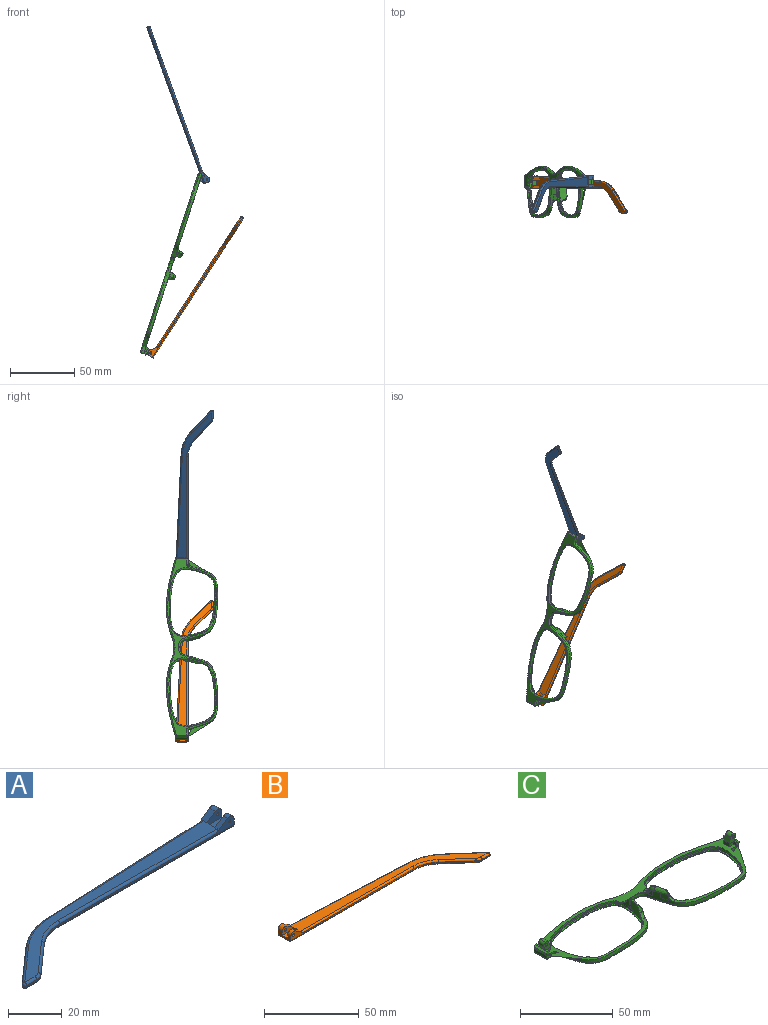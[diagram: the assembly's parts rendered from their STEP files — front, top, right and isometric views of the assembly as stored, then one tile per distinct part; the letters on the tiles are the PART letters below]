
ASSEMBLY  parts=3 mates=2
PART A: 43 faces, bbox 130.2x29.5x5.9 mm
  f0: plane 9.62x3.72mm, normal (1,0,0), area 24.7mm2, adj f1,f3,f4,f5,f10,f16,f18,f28
  f1: cylinder r=2.2mm len=3.45mm, axis (0,-1,0), area 11mm2, adj f0,f2,f4,f37
  f2: plane 6.01x3.91mm, normal (-0.55,0,0.84), area 12.7mm2, adj f1,f4,f9,f19,f37
  f3: plane 2.26x0.1mm, normal (0,0,1), area 0.1mm2, adj f0,f5,f18
  f4: plane 92.1x4.9mm, normal (0,-1,0), area 79.9mm2, adj f0,f1,f2,f14,f19,f36,f42
  f5: plane 93.42x4.13mm, normal (-0.04,1,0), area 64.8mm2, adj f0,f3,f11,f15,f17,f27,f28
  f6: plane 17.82x15.72mm, normal (-0.66,0.75,0), area 14.3mm2, adj f11,f12,f25,f30
  f7: plane 5.46x0.6mm, normal (0,-1,0), area 3.3mm2, adj f12,f13,f23,f32
  f8: plane 14.99x13.23mm, normal (0.66,-0.75,0), area 12mm2, adj f13,f14,f21,f34
  f9: plane 121.18x26.73mm, normal (0,0,1), area 627.7mm2, adj f2,f17,f19,f20,f21,f22,f23,f25
  f10: plane 129.1x27.08mm, normal (0,0,-1), area 686.5mm2, adj f0,f28,f29,f30,f32,f33,f34,f35
  f11: cylinder r=30mm len=18.52mm, axis (0,0,-1), area 12.2mm2, adj f5,f6,f26,f29
  f12: cylinder r=1mm len=1.75mm, axis (0,0,-1), area 1.5mm2, adj f6,f7,f24,f31
  f13: cylinder r=5mm len=3.31mm, axis (0,0,-1), area 2.2mm2, adj f7,f8,f22,f33
  f14: cylinder r=20mm len=13.23mm, axis (0,0,1), area 8.7mm2, adj f4,f8,f20,f35
  f15: plane 5.66x0.25mm, normal (0,0,-1), area 0.7mm2, adj f5,f17,f18
  f16: cylinder r=2.2mm len=3.45mm, axis (0,-1,0), area 14.8mm2, adj f0,f17,f18,f38
  f17: plane 6.01x3.91mm, normal (-0.55,0,0.84), area 16.9mm2, adj f5,f9,f15,f16,f18,f27,f38
  f18: plane 7.92x3.3mm, normal (0,1,0), area 15.9mm2, adj f0,f3,f15,f16,f17,f41
  f19: cylinder r=1mm len=84.18mm, axis (-1,0,0), area 131.4mm2, adj f2,f4,f9,f20
  f20: torus R=21mm, axis (0,0,1), area 23.1mm2, adj f9,f14,f19,f21
  f21: cylinder r=1mm len=15.65mm, axis (-0.75,-0.66,0), area 31.4mm2, adj f8,f9,f20,f22
  f22: torus R=4mm, axis (0,0,1), area 5.3mm2, adj f9,f13,f21,f23
  f23: cylinder r=1mm len=5.46mm, axis (-1,0,0), area 8.6mm2, adj f7,f9,f22,f24
  f24: sphere r=1mm, area 2.4mm2, adj f12,f23,f25
  f25: cylinder r=1mm len=18.48mm, axis (0.75,0.66,0), area 37.3mm2, adj f6,f9,f24,f26
  f26: torus R=29mm, axis (0,0,1), area 31.6mm2, adj f9,f11,f25,f27
  f27: cylinder r=1mm len=85.5mm, axis (1,0.04,0), area 133.5mm2, adj f5,f9,f17,f26
  f28: cylinder r=1mm len=93.46mm, axis (-1,-0.04,0), area 146.9mm2, adj f0,f5,f10,f29
  f29: torus R=29mm, axis (0,0,1), area 31.6mm2, adj f10,f11,f28,f30
  f30: cylinder r=1mm len=18.48mm, axis (-0.75,-0.66,0), area 37.3mm2, adj f6,f10,f29,f31
  f31: sphere r=1mm, area 2.4mm2, adj f12,f30,f32
  f32: cylinder r=1mm len=5.46mm, axis (1,0,0), area 8.6mm2, adj f7,f10,f31,f33
  f33: torus R=4mm, axis (0,0,1), area 5.3mm2, adj f10,f13,f32,f34
  f34: cylinder r=1mm len=15.65mm, axis (0.75,0.66,0), area 31.4mm2, adj f8,f10,f33,f35
  f35: torus R=21mm, axis (0,0,1), area 23.1mm2, adj f10,f14,f34,f36
  f36: cylinder r=1mm len=92.1mm, axis (1,0,0), area 144.7mm2, adj f0,f4,f10,f35
  f37: plane 7.92x4.7mm, normal (0,1,0), area 27mm2, adj f0,f1,f2,f39,f40,f42
  f38: plane 7.92x4.7mm, normal (0,-1,0), area 27mm2, adj f0,f16,f17,f39,f40,f41
  f39: plane 7.92x4.1mm, normal (0,0,1), area 32.5mm2, adj f0,f37,f38,f40
  f40: plane 4.1x1.4mm, normal (1,0,0), area 5.7mm2, adj f9,f37,f38,f39
  f41: cylinder r=0.5mm len=3.1mm, axis (0,-1,0), area 9.7mm2, adj f18,f38
  f42: cylinder r=0.5mm len=2.3mm, axis (0,-1,0), area 7.2mm2, adj f4,f37
PART B: 43 faces, bbox 130.2x29.5x5.9 mm
  f0: plane 9.62x3.72mm, normal (-1,0,0), area 24.7mm2, adj f1,f3,f4,f5,f10,f16,f18,f28
  f1: cylinder r=2.2mm len=3.45mm, axis (0,-1,0), area 11mm2, adj f0,f2,f4,f37
  f2: plane 6.01x3.91mm, normal (0.55,0,0.84), area 12.7mm2, adj f1,f4,f9,f19,f37
  f3: plane 2.26x0.1mm, normal (0,0,1), area 0.1mm2, adj f0,f5,f18
  f4: plane 92.1x4.9mm, normal (0,-1,0), area 78.2mm2, adj f0,f1,f2,f14,f19,f36,f42
  f5: plane 93.42x4.13mm, normal (0.04,1,0), area 64.8mm2, adj f0,f3,f11,f15,f17,f27,f28
  f6: plane 17.82x15.72mm, normal (0.66,0.75,0), area 14.3mm2, adj f11,f12,f25,f30
  f7: plane 5.46x0.6mm, normal (0,-1,0), area 3.3mm2, adj f12,f13,f23,f32
  f8: plane 14.99x13.23mm, normal (-0.66,-0.75,0), area 12mm2, adj f13,f14,f21,f34
  f9: plane 121.18x26.73mm, normal (0,0,1), area 627.7mm2, adj f2,f17,f19,f20,f21,f22,f23,f25
  f10: plane 129.1x27.08mm, normal (0,0,-1), area 686.5mm2, adj f0,f28,f29,f30,f32,f33,f34,f35
  f11: cylinder r=30mm len=18.52mm, axis (0,0,-1), area 12.2mm2, adj f5,f6,f26,f29
  f12: cylinder r=1mm len=1.75mm, axis (0,0,-1), area 1.5mm2, adj f6,f7,f24,f31
  f13: cylinder r=5mm len=3.31mm, axis (0,0,-1), area 2.2mm2, adj f7,f8,f22,f33
  f14: cylinder r=20mm len=13.23mm, axis (0,0,1), area 8.7mm2, adj f4,f8,f20,f35
  f15: plane 5.66x0.25mm, normal (0,0,-1), area 0.7mm2, adj f5,f17,f18
  f16: cylinder r=2.2mm len=3.45mm, axis (0,-1,0), area 14.8mm2, adj f0,f17,f18,f38
  f17: plane 6.01x3.91mm, normal (0.55,0,0.84), area 16.9mm2, adj f5,f9,f15,f16,f18,f27,f38
  f18: plane 7.92x3.3mm, normal (0,1,0), area 14.3mm2, adj f0,f3,f15,f16,f17,f41
  f19: cylinder r=1mm len=84.18mm, axis (1,0,0), area 131.4mm2, adj f2,f4,f9,f20
  f20: torus R=21mm, axis (0,0,1), area 23.1mm2, adj f9,f14,f19,f21
  f21: cylinder r=1mm len=15.65mm, axis (0.75,-0.66,0), area 31.4mm2, adj f8,f9,f20,f22
  f22: torus R=4mm, axis (0,0,1), area 5.3mm2, adj f9,f13,f21,f23
  f23: cylinder r=1mm len=5.46mm, axis (1,0,0), area 8.6mm2, adj f7,f9,f22,f24
  f24: sphere r=1mm, area 2.4mm2, adj f12,f23,f25
  f25: cylinder r=1mm len=18.48mm, axis (-0.75,0.66,0), area 37.3mm2, adj f6,f9,f24,f26
  f26: torus R=29mm, axis (0,0,1), area 31.6mm2, adj f9,f11,f25,f27
  f27: cylinder r=1mm len=85.5mm, axis (-1,0.04,0), area 133.5mm2, adj f5,f9,f17,f26
  f28: cylinder r=1mm len=93.46mm, axis (1,-0.04,0), area 146.9mm2, adj f0,f5,f10,f29
  f29: torus R=29mm, axis (0,0,1), area 31.6mm2, adj f10,f11,f28,f30
  f30: cylinder r=1mm len=18.48mm, axis (0.75,-0.66,0), area 37.3mm2, adj f6,f10,f29,f31
  f31: sphere r=1mm, area 2.4mm2, adj f12,f30,f32
  f32: cylinder r=1mm len=5.46mm, axis (-1,0,0), area 8.6mm2, adj f7,f10,f31,f33
  f33: torus R=4mm, axis (0,0,1), area 5.3mm2, adj f10,f13,f32,f34
  f34: cylinder r=1mm len=15.65mm, axis (-0.75,0.66,0), area 31.4mm2, adj f8,f10,f33,f35
  f35: torus R=21mm, axis (0,0,1), area 23.1mm2, adj f10,f14,f34,f36
  f36: cylinder r=1mm len=92.1mm, axis (-1,0,0), area 144.7mm2, adj f0,f4,f10,f35
  f37: plane 7.92x4.7mm, normal (0,1,0), area 25.4mm2, adj f0,f1,f2,f39,f40,f42
  f38: plane 7.92x4.7mm, normal (0,-1,0), area 25.4mm2, adj f0,f16,f17,f39,f40,f41
  f39: plane 7.92x4.1mm, normal (0,0,1), area 32.5mm2, adj f0,f37,f38,f40
  f40: plane 4.1x1.4mm, normal (-1,0,0), area 5.7mm2, adj f9,f37,f38,f39
  f41: cylinder r=0.88mm len=3.1mm, axis (0,-1,0), area 17mm2, adj f18,f38
  f42: cylinder r=0.88mm len=2.3mm, axis (0,-1,0), area 12.6mm2, adj f4,f37
PART C: 118 faces, bbox 148.1x40.9x18 mm
  f0: bspline ~1.82x1.22mm, area 0.7mm2, adj f2,f7,f37,f52
  f1: plane 147.73x40.5mm, normal (0,0,1), area 772.9mm2, adj f4,f5,f6,f7,f8,f12,f20,f23
  f2: bspline ~5.39x4.93mm, area 12.7mm2, adj f0,f7,f37,f41,f43,f52,f53
  f3: plane 4.46x1.45mm, normal (0,0,1), area 0.1mm2, adj f7,f38
  f4: plane 1.23x0.04mm, normal (0,0,1), area 0mm2, adj f1,f7,f22
  f5: plane 6.97x5.07mm, normal (0,1,0), area 22.7mm2, adj f1,f20,f21,f25,f27,f28,f30,f31
  f6: plane 3.2x2.36mm, normal (0,-1,0), area 5.7mm2, adj f1,f20,f26,f29
  f7: extruded ~73.26x39.84mm, area 292.7mm2, adj f0,f1,f2,f3,f4,f8,f13,f14
  f8: extruded ~35.39x5.69mm, area 72.2mm2, adj f1,f7,f18,f67
  f9: plane 144.78x37.85mm, normal (0,0,-1), area 478.1mm2, adj f13,f15,f17,f18,f19,f71,f73,f75
  f10: plane 56.31x36.53mm, normal (0,0,1), area 124.8mm2, adj f11,f19
  f11: extruded ~55.63x36.1mm, area 160.7mm2, adj f10,f12
  f12: extruded ~55.63x36.1mm, area 220.4mm2, adj f1,f11,f39,f40,f41,f42,f43,f44
  f13: bspline ~73.27x30.39mm, area 161.7mm2, adj f7,f9,f14,f71
  f14: bspline ~1x1mm, area 0.8mm2, adj f7,f13,f15
  f15: bspline ~8.99x1.23mm, area 12.6mm2, adj f7,f9,f14,f16
  f16: bspline ~1.04x1mm, area 0.7mm2, adj f7,f15,f17
  f17: bspline ~45.86x8.59mm, area 59.8mm2, adj f7,f9,f16,f18
  f18: bspline ~37.01x6.7mm, area 56.6mm2, adj f8,f9,f17,f76
  f19: bspline ~56.15x36.68mm, area 237.6mm2, adj f9,f10
  f20: plane 4x2.36mm, normal (-1,0,0), area 9.5mm2, adj f1,f5,f6,f21
  f21: plane 4x0.02mm, normal (0.34,0,0.94), area 0.1mm2, adj f5,f20,f28
  f22: plane 2.76x2.53mm, normal (0,-1,0), area 3.9mm2, adj f4,f26,f27,f35,f56
  f23: plane 7.67x1.6mm, normal (0.94,0,-0.34), area 13mm2, adj f1,f35,f36,f56
  f24: plane 2.1x1.69mm, normal (0,1,0), area 2.8mm2, adj f1,f25,f27,f36,f56
  f25: plane 3.3x2.1mm, normal (-1,0,0), area 6.9mm2, adj f1,f5,f24,f27
  f26: plane 2.35x2.1mm, normal (-1,0,0), area 4.9mm2, adj f1,f6,f22,f27,f29
  f27: plane 9.65x1.24mm, normal (0,0,1), area 8.2mm2, adj f5,f22,f24,f25,f26,f29,f30,f56
  f28: plane 4x3.31mm, normal (-0.94,0,0.34), area 14.1mm2, adj f5,f21,f29,f32
  f29: plane 5.77x5.06mm, normal (0,-1,0), area 17mm2, adj f6,f26,f27,f28,f30,f31,f32,f33
  f30: plane 4x2.21mm, normal (0.94,0,-0.34), area 9.4mm2, adj f5,f27,f29,f33
  f31: plane 4x0.01mm, normal (0.34,0,0.94), area 0mm2, adj f5,f29,f32,f33
  f32: cylinder r=1.98mm len=4mm, axis (0,1,0), area 12.4mm2, adj f5,f28,f29,f31
  f33: cylinder r=1.98mm len=4mm, axis (0,-1,0), area 12.4mm2, adj f5,f29,f30,f31
  f34: cylinder r=0.88mm len=4mm, axis (0,-1,0), area 22mm2, adj f5,f29
  f35: cone r=1mm half-angle=20deg, axis (0,0,1), area 2.3mm2, adj f1,f22,f23,f56
  f36: cylinder r=1mm len=2.28mm, axis (-0.34,0,-0.94), area 3mm2, adj f1,f23,f24,f56
  f37: extruded ~3.67x3.11mm, area 5.9mm2, adj f0,f2,f7,f59
  f38: extruded ~4.44x3.32mm, area 15.1mm2, adj f3,f7,f42,f43,f55
  f39: extruded ~4.98x1.36mm, area 6.6mm2, adj f12,f41
  f40: plane 3.63x0.97mm, normal (0,0,1), area 0.3mm2, adj f12,f41,f43
  f41: bspline ~15.5x15.35mm, area 6.4mm2, adj f2,f12,f39,f40,f54
  f42: bspline ~7.26x7.26mm, area 6.3mm2, adj f12,f38,f43,f55
  f43: bspline ~10.29x4.84mm, area 21.4mm2, adj f2,f7,f12,f38,f40,f42
  f44: plane 2.88x1.51mm, normal (0,0,-1), area 1.8mm2, adj f12,f45
  f45: cylinder r=2.28mm len=2.86mm, axis (0,0,1), area 1.8mm2, adj f1,f12,f44,f54
  f46: plane 2.5x1.83mm, normal (0,0,-1), area 1.7mm2, adj f12,f47
  f47: cylinder r=2.28mm len=2.47mm, axis (0,0,1), area 1.7mm2, adj f1,f12,f46
  f48: plane 1.79x1.31mm, normal (0,0,-1), area 0.9mm2, adj f12,f49
  f49: cylinder r=1.3mm len=1.78mm, axis (0,0,1), area 1.3mm2, adj f1,f12,f48
  f50: plane 1.95x1.68mm, normal (0,0,-1), area 1.5mm2, adj f12,f51
  f51: cylinder r=1.3mm len=1.93mm, axis (0,0,1), area 1.5mm2, adj f1,f12,f50
  f52: bspline ~2.66x2.04mm, area 1.9mm2, adj f0,f2,f7,f53,f58
  f53: bspline ~3.55x3.47mm, area 3.7mm2, adj f1,f2,f52,f54,f58
  f54: bspline ~5.1x3.97mm, area 7.6mm2, adj f1,f12,f41,f45,f53
  f55: bspline ~3.7x3.66mm, area 7.8mm2, adj f1,f7,f12,f38,f42
  f56: plane 9.71x1.44mm, normal (0.34,0,0.94), area 13.9mm2, adj f22,f23,f24,f27,f35,f36
  f57: bspline ~6.38x2.14mm, area 2.6mm2, adj f1,f7,f58,f115
  f58: bspline ~2.1x1.46mm, area 0.6mm2, adj f7,f52,f53,f57
  f59: bspline ~5.24x1.75mm, area 0mm2, adj f7,f37
  f60: bspline ~2.19x1.4mm, area 0.7mm2, adj f61,f66,f95,f110
  f61: bspline ~6.1x4.93mm, area 12.6mm2, adj f60,f66,f95,f99,f101,f110,f111
  f62: plane 4.46x1.45mm, normal (0,0,1), area 0.1mm2, adj f66,f96
  f63: plane 1.23x0.04mm, normal (0,0,1), area 0mm2, adj f1,f66,f80
  f64: plane 6.97x5.07mm, normal (0,1,0), area 22.7mm2, adj f1,f78,f79,f83,f85,f86,f88,f89
  f65: plane 3.2x2.36mm, normal (0,-1,0), area 5.7mm2, adj f1,f78,f84,f87
  f66: extruded ~73.26x39.84mm, area 292.7mm2, adj f1,f7,f60,f61,f62,f63,f67,f71
  f67: extruded ~35.39x5.69mm, area 72.2mm2, adj f1,f8,f66,f76
  f68: plane 56.31x36.53mm, normal (0,0,1), area 124.8mm2, adj f69,f77
  f69: extruded ~55.63x36.1mm, area 160.7mm2, adj f68,f70
  f70: extruded ~55.63x36.1mm, area 220.4mm2, adj f1,f69,f97,f98,f99,f100,f101,f102
  f71: bspline ~73.83x30.39mm, area 161.7mm2, adj f9,f13,f66,f72
  f72: bspline ~1x1mm, area 0.8mm2, adj f66,f71,f73
  f73: bspline ~8.99x1.23mm, area 12.6mm2, adj f9,f66,f72,f74
  f74: bspline ~1.04x1mm, area 0.8mm2, adj f66,f73,f75
  f75: bspline ~45.86x8.59mm, area 59.8mm2, adj f9,f66,f74,f76
  f76: bspline ~37.01x6.7mm, area 56.6mm2, adj f9,f18,f67,f75
  f77: bspline ~56.15x36.68mm, area 237.6mm2, adj f9,f68
  f78: plane 4x2.36mm, normal (1,0,0), area 9.5mm2, adj f1,f64,f65,f79
  f79: plane 4x0.02mm, normal (-0.34,0,0.94), area 0.1mm2, adj f64,f78,f86
  f80: plane 2.76x2.53mm, normal (0,-1,0), area 3.9mm2, adj f63,f84,f85,f93,f114
  f81: plane 7.67x1.6mm, normal (-0.94,0,-0.34), area 13mm2, adj f1,f93,f94,f114
  f82: plane 2.1x1.69mm, normal (0,1,0), area 2.8mm2, adj f1,f83,f85,f94,f114
  f83: plane 3.3x2.1mm, normal (1,0,0), area 6.9mm2, adj f1,f64,f82,f85
  f84: plane 2.35x2.1mm, normal (1,0,0), area 4.9mm2, adj f1,f65,f80,f85,f87
  f85: plane 9.65x1.24mm, normal (0,0,1), area 8.2mm2, adj f64,f80,f82,f83,f84,f87,f88,f114
  f86: plane 4x3.31mm, normal (0.94,0,0.34), area 14.1mm2, adj f64,f79,f87,f90
  f87: plane 5.77x5.06mm, normal (0,-1,0), area 17mm2, adj f65,f84,f85,f86,f88,f89,f90,f91
  f88: plane 4x2.21mm, normal (-0.94,0,-0.34), area 9.4mm2, adj f64,f85,f87,f91
  f89: plane 4x0.01mm, normal (-0.34,0,0.94), area 0mm2, adj f64,f87,f90,f91
  f90: cylinder r=1.98mm len=4mm, axis (0,1,0), area 12.4mm2, adj f64,f86,f87,f89
  f91: cylinder r=1.98mm len=4mm, axis (0,-1,0), area 12.4mm2, adj f64,f87,f88,f89
  f92: cylinder r=0.88mm len=4mm, axis (0,-1,0), area 22mm2, adj f64,f87
  f93: cone r=1mm half-angle=20deg, axis (0,0,1), area 2.3mm2, adj f1,f80,f81,f114
  f94: cylinder r=1mm len=2.28mm, axis (0.34,0,-0.94), area 3mm2, adj f1,f81,f82,f114
  f95: extruded ~3.67x3.11mm, area 5.9mm2, adj f60,f61,f66,f117
  f96: extruded ~4.44x3.32mm, area 15.1mm2, adj f62,f66,f100,f101,f113
  f97: extruded ~4.98x1.36mm, area 6.6mm2, adj f70,f99
  f98: plane 3.63x0.97mm, normal (0,0,1), area 0.3mm2, adj f70,f99,f101
  f99: bspline ~15.5x15.35mm, area 6.4mm2, adj f61,f70,f97,f98,f112
  f100: bspline ~7.26x7.26mm, area 6.2mm2, adj f70,f96,f101,f113
  f101: bspline ~10.29x4.84mm, area 21.5mm2, adj f61,f66,f70,f96,f98,f100
  f102: plane 2.88x1.51mm, normal (0,0,-1), area 1.8mm2, adj f70,f103
  f103: cylinder r=2.28mm len=2.86mm, axis (0,0,1), area 1.8mm2, adj f1,f70,f102,f112
  f104: plane 2.5x1.83mm, normal (0,0,-1), area 1.7mm2, adj f70,f105
  f105: cylinder r=2.28mm len=2.47mm, axis (0,0,1), area 1.7mm2, adj f1,f70,f104
  f106: plane 1.79x1.31mm, normal (0,0,-1), area 0.9mm2, adj f70,f107
  f107: cylinder r=1.3mm len=1.78mm, axis (0,0,1), area 1.3mm2, adj f1,f70,f106
  f108: plane 1.95x1.68mm, normal (0,0,-1), area 1.5mm2, adj f70,f109
  f109: cylinder r=1.3mm len=1.93mm, axis (0,0,1), area 1.5mm2, adj f1,f70,f108
  f110: bspline ~2.65x2.03mm, area 1.9mm2, adj f60,f61,f66,f111,f116
  f111: bspline ~3.55x3.47mm, area 3.7mm2, adj f1,f61,f110,f112,f116
  f112: bspline ~4.88x3.94mm, area 7.6mm2, adj f1,f70,f99,f103,f111
  f113: bspline ~3.7x3.66mm, area 7.8mm2, adj f1,f66,f70,f96,f100
  f114: plane 9.71x1.44mm, normal (-0.34,0,0.94), area 13.9mm2, adj f80,f81,f82,f85,f93,f94
  f115: bspline ~6.38x2.14mm, area 2.6mm2, adj f1,f57,f66,f116
  f116: bspline ~2.1x1.46mm, area 0.6mm2, adj f66,f110,f111,f115
  f117: bspline ~5.24x1.75mm, area 0mm2, adj f66,f95
PLACE A rot(axis=(0,1,0),70deg) t=(98.49,-5.75,193.6)mm
PLACE B rot(axis=(0,-1,0),57deg) t=(46.73,-5.75,-52.07)mm
PLACE C rot(axis=(0,1,0),108deg) t=(93.78,-1.13,73.41)mm
MATE revolute A.f1 <-> C.f90  axis (0,-1,0) through (122.37,2.72,138.82)mm
MATE revolute B.f41 <-> C.f33  axis (0,-1,0) through (78.48,2.72,3.68)mm
